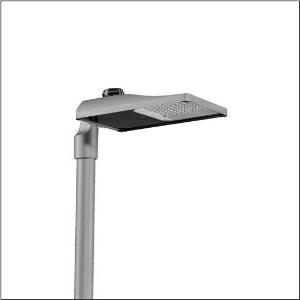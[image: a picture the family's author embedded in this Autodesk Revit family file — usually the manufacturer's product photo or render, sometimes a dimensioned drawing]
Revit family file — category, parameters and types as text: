
# Revit family: streetlight_sl_31_midi___pl52_5xh7h75n08la_2e4f
name_source: partatom
category: Lighting Fixtures
units: mm (PartAtom-declared; Revit-internal decimal feet)

## family parameters
Cut with Voids When Loaded = No
Host = Face
Light Source = No
Part Type = Normal
Room Calculation Point = No
Round Connector Dimension = Use Diameter
Shared = No

## types (1)
- --- (1 x LED, 10460 lm, 86.6 W, 2200K)
    Apparent Load = 87 VA
    CIE Flux Codes = 27 59 98 100 100
    Color Rendering = 70
    Color Temperature = 2200K
    Default Elevation = 1800 mm
    Description = Streetlight SL 31 midi NEMA (7pin), Desk-Remote mast luminaire for post-top, side-entry; light control with lens of PMMA; light distribution: PL52, direct asymmetric distribution, for standard-compliant lighting for roads and squares; LED: luminous flux: 10.460lm, light colour: 722, colour temperature: 2200K; luminous efficacy: 120,8lm/W; control: pre-setting: linear dimming characteristic, flexible luminous flux parameterisation, time-dependent luminous flux control, constant luminous flux control, intelligent temperature release in ECG and LED module, overheat protection; luminaire housing, of diecast aluminium, SITECO metallic grey (DB 702S), corrosivity category C5 high according to DIN EN ISO 12944; cover of toughened safety glass, transparent, opened without tools; mast flange of diecast aluminium, SITECO metallic grey (DB 702S), spigot size: 76/60mm, mast flange included unmounted; cable length: 10,5m, connection cable pre-assembled; mains connection: 220..240V, AC, 50/60Hz; power consumption (at start of service life): 86,6W / (at end of service life): 90W / (with reduced operation 50%): 39,8W; protection rating (complete): IP66; insulation class (complete): insulation class I (protective earthing); impact resistance: IK10; certification: CE, ENEC, ENEC+, VDE, UKCA; permissible operating ambient temperature for outdoor applications: -40..+50°C; packaging unit: 1 piece

Light Distribution: PL52
    Height = 79 mm
    Lamp = 1 x LED
    Lamp Light Flux = 10460 lm
    Lamp Power = 86.6 W
    Lamp count = 1
    Length = 577 mm
    Luminous efficacy = 121 lm/W
    Manufacturer = Siteco
    ModVariant = No
    Model = 5XH7H75N08LA
    Number of Poles = 1
    OnlyDefault = Yes
    Power Factor = 1
    Product Name = Streetlight SL 31 midi | PL52
    Product group = mast luminaire | pylon top
    ProductGroupID = 6100
    Protection Class = Protection class I
    Protection Degree = IP 66
    RLX_Detail_Level = 1
    RLX_Emergency_Light_Flux = 0 lm
    RLX_Emergency_Type = 0
    RLX_Emergency_Type_DB = No
    RlxData = <blob elided: 35761 chars, md5=3ba000b4>
    Socket = socket
    Standby Power = 0 W
    System Light Flux = 10460 lm
    System Power = 87 W
    Type Comments = factory setting: luminous flux: 100 % | dim-lin: 254 | 456 mA
    Type Image = l_1300282.jpg
    URL = http://relux.com
    VarID = @adj_009739
    Voltage = 0 V
    Weight = 0.00 kg
    Width = 362 mm

## geometry (parser evidence)
native form markers: Blend x4, Sweep x10
no freeform markers — native parametric forms only
